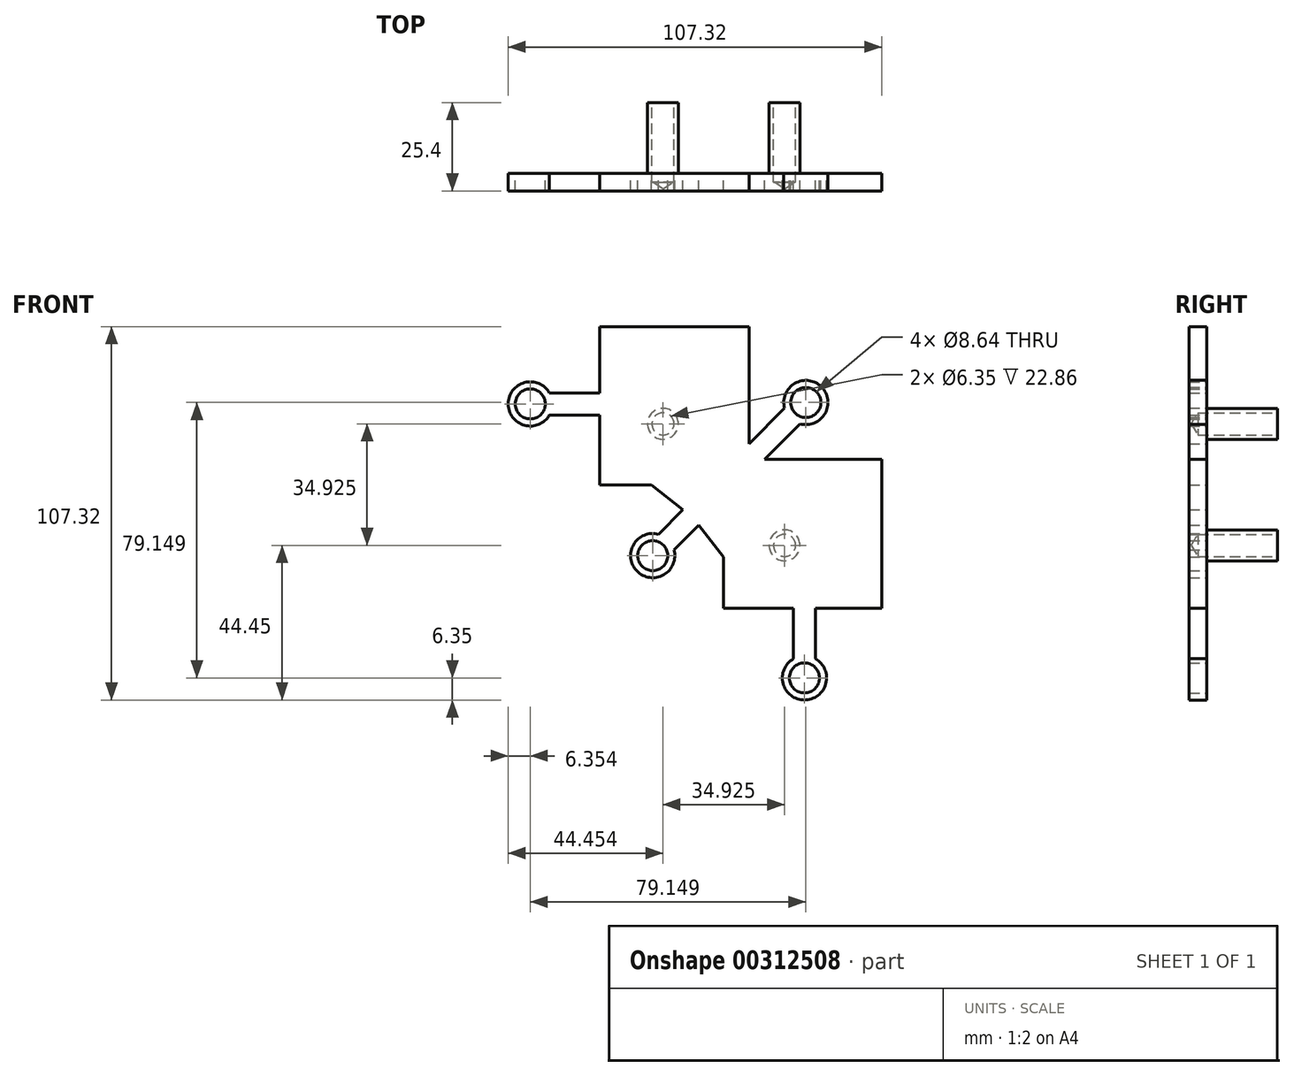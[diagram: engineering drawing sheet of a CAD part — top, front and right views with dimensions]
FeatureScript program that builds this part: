
annotation { "Feature Type Name" : "Feature", "Feature Type Description" : "" }
export const myFeature = defineFeature(function(context is Context, id is Id, definition is map)
    precondition{}
    {
        {
            var Q0;
            Q0=qCreatedBy(makeId("Front.planeOp"),FACE);
            var sketch = newSketch(context, id + "F0", { "sketchPlane" : qUnion([Q0])});
            skArc(sketch, "E0", {"start": v(27.13, 27.65) * mm, "mid": v(33.26, 38.27) * mm, "end": v(22.64, 32.14) * mm});
            skLineSegment(sketch, "E1.0", {"start": v(12.42, 21.92) * mm, "end": v(22.64, 32.14) * mm});
            skLineSegment(sketch, "E2.0", {"start": v(16.9, 17.43) * mm, "end": v(27.13, 27.65) * mm});
            skArc(sketch, "E3", {"start": v(-44.88, 36.55) * mm, "mid": v(-56.73, 33.37) * mm, "end": v(-44.88, 30.2) * mm});
            skArc(sketch, "E4", {"start": v(-13.58, -4.09) * mm, "mid": v(-19.71, -14.7) * mm, "end": v(-9.1, -8.58) * mm});
            skArc(sketch, "E5", {"start": v(25.19, -39.87) * mm, "mid": v(28.36, -51.72) * mm, "end": v(31.54, -39.87) * mm});
            skLineSegment(sketch, "E6.0", {"start": v(-44.88, 30.2) * mm, "end": v(-30.4, 30.2) * mm});
            skLineSegment(sketch, "E7.MirrorCS", {"start": v(25.19, -39.87) * mm, "end": v(25.19, -25.4) * mm});
            skArc(sketch, "E8.MirrorCS", {"start": v(31.54, -39.87) * mm, "mid": v(28.36, -51.72) * mm, "end": v(25.19, -39.87) * mm});
            skLineSegment(sketch, "E9", {"start": v(12.42, 36.55) * mm, "end": v(12.42, 21.92) * mm});
            skPoint(sketch, "E10.start.orphan", {"position": v(-7.83, 27.66) * mm});
            skLineSegment(sketch, "E11", {"start": v(31.54, 17.43) * mm, "end": v(16.9, 17.43) * mm});
            skPoint(sketch, "E12.start.orphan", {"position": v(22.65, -2.82) * mm});
            skLineSegment(sketch, "E13", {"start": v(31.54, -25.4) * mm, "end": v(31.54, -39.87) * mm});
            skLineSegment(sketch, "E14", {"start": v(-30.4, 36.55) * mm, "end": v(-44.88, 36.55) * mm});
            skLineSegment(sketch, "E15", {"start": v(-6.52, 2.97) * mm, "end": v(-15.61, 10.05) * mm});
            skPoint(sketch, "E15.endSnap0", {"position": v(-15.61, 24.72) * mm});
            skLineSegment(sketch, "E16", {"start": v(-15.61, 10.05) * mm, "end": v(-30.4, 10.05) * mm});
            skPoint(sketch, "E16.endSnap0", {"position": v(-30.4, 30.2) * mm});
            skLineSegment(sketch, "E17", {"start": v(-30.4, 16.4) * mm, "end": v(-30.4, 30.2) * mm});
            skCircle(sketch, "E18", {"center": v(-12.28, 27.66) * mm, "radius": 4.45 * mm});
            skLineSegment(sketch, "E19.MirrorCS", {"start": v(-2.03, -1.52) * mm, "end": v(5.05, -10.6) * mm});
            skLineSegment(sketch, "E20.MirrorCS", {"start": v(5.05, -10.6) * mm, "end": v(5.05, -25.4) * mm});
            skLineSegment(sketch, "E21.MirrorCS", {"start": v(11.4, -25.4) * mm, "end": v(25.19, -25.4) * mm});
            skCircle(sketch, "E22", {"center": v(22.65, -7.27) * mm, "radius": 4.45 * mm});
            skLineSegment(sketch, "E23.0", {"start": v(-9.1, -8.58) * mm, "end": v(-2.03, -1.52) * mm});
            skLineSegment(sketch, "E24.0", {"start": v(-13.58, -4.09) * mm, "end": v(-6.52, 2.97) * mm});
            skLineSegment(sketch, "E25", {"start": v(12.42, 36.55) * mm, "end": v(12.42, 55.6) * mm});
            skLineSegment(sketch, "E26", {"start": v(12.42, 55.6) * mm, "end": v(-30.4, 55.6) * mm});
            skLineSegment(sketch, "E27", {"start": v(-30.4, 55.6) * mm, "end": v(-30.4, 36.55) * mm});
            skLineSegment(sketch, "E28", {"start": v(-15.22, -10.22) * mm, "end": v(28.77, 33.78) * mm});
            skLineSegment(sketch, "E29.MirrorCS", {"start": v(50.59, 17.43) * mm, "end": v(50.59, -25.4) * mm});
            skLineSegment(sketch, "E30.MirrorCS", {"start": v(31.54, 17.43) * mm, "end": v(50.59, 17.43) * mm});
            skLineSegment(sketch, "E31.MirrorCS", {"start": v(50.59, -25.4) * mm, "end": v(31.54, -25.4) * mm});
            skLineSegment(sketch, "E32", {"start": v(-30.4, 16.4) * mm, "end": v(-30.4, 10.05) * mm});
            skLineSegment(sketch, "E33", {"start": v(5.05, -25.4) * mm, "end": v(11.4, -25.4) * mm});
            skPoint(sketch, "E34.end.orphan", {"position": v(-62.5, 16.4) * mm});
            skPoint(sketch, "E35.end.orphan", {"position": v(-62.5, -0.1) * mm});
            skPoint(sketch, "E36.end.orphan", {"position": v(-30.76, -0.1) * mm});
            skPoint(sketch, "E37.MirrorCS.end.orphan", {"position": v(-5.1, -25.75) * mm});
            skPoint(sketch, "E37.MirrorCS.start.orphan", {"position": v(5.05, -25.4) * mm});
            skPoint(sketch, "E38.MirrorCS.end.orphan", {"position": v(-5.1, -57.5) * mm});
            skPoint(sketch, "E39.MirrorCS.end.orphan", {"position": v(11.4, -57.5) * mm});
            skSolve(sketch);
        }
        {
            var Q0;
            Q0=makeQuery(id+"F0.imprint","IMPRINT",FACE,{"disambiguationData":[TD([[makeQuery(id+"F0.imprint","IMPRINT",EDGE,{"derivedFrom":sQuery(id+"F0.wireOp",EDGE,"E0")}),1.0]])]});
            extrude(context, id + "F1", {"entities" : qUnion([Q0]), "depth" : 5.08 * mm, "offsetDistance" : 25.4 * mm});
        }
        {
            var Q0;
            Q0=makeQuery(id+"F1.opExtrude","CAP_FACE",FACE,{"disambiguationData":[OSD([sQuery(id+"F0.wireOp",EDGE,"E0"),sQuery(id+"F0.wireOp",EDGE,"E1.0"),sQuery(id+"F0.wireOp",EDGE,"E2.0"),sQuery(id+"F0.wireOp",EDGE,"E3"),sQuery(id+"F0.wireOp",EDGE,"E4"),sQuery(id+"F0.wireOp",EDGE,"E6.0"),sQuery(id+"F0.wireOp",EDGE,"E7.MirrorCS"),sQuery(id+"F0.wireOp",EDGE,"E8.MirrorCS"),sQuery(id+"F0.wireOp",EDGE,"E9"),sQuery(id+"F0.wireOp",EDGE,"E11"),sQuery(id+"F0.wireOp",EDGE,"E13"),sQuery(id+"F0.wireOp",EDGE,"E14"),sQuery(id+"F0.wireOp",EDGE,"E15"),sQuery(id+"F0.wireOp",EDGE,"E16"),sQuery(id+"F0.wireOp",EDGE,"E17"),sQuery(id+"F0.wireOp",EDGE,"E18"),sQuery(id+"F0.wireOp",EDGE,"E19.MirrorCS"),sQuery(id+"F0.wireOp",EDGE,"E20.MirrorCS"),sQuery(id+"F0.wireOp",EDGE,"E21.MirrorCS"),sQuery(id+"F0.wireOp",EDGE,"E22"),sQuery(id+"F0.wireOp",EDGE,"E23.0"),sQuery(id+"F0.wireOp",EDGE,"E24.0"),sQuery(id+"F0.wireOp",EDGE,"E25"),sQuery(id+"F0.wireOp",EDGE,"E26"),sQuery(id+"F0.wireOp",EDGE,"E27"),sQuery(id+"F0.wireOp",EDGE,"E29.MirrorCS"),sQuery(id+"F0.wireOp",EDGE,"E30.MirrorCS"),sQuery(id+"F0.wireOp",EDGE,"E31.MirrorCS"),sQuery(id+"F0.wireOp",EDGE,"E32"),sQuery(id+"F0.wireOp",EDGE,"E33")])],"isStart":false});
            var sketch = newSketch(context, id + "F2", { "sketchPlane" : qUnion([Q0])});
            skCircle(sketch, "E40", {"center": v(-12.28, 27.66) * mm, "radius": 4.45 * mm});
            skCircle(sketch, "E41", {"center": v(22.65, -7.27) * mm, "radius": 4.45 * mm});
            skSolve(sketch);
        }
        {
            var Q0;
            Q0=makeQuery(id+"F2.imprint","IMPRINT",FACE,{"disambiguationData":[TD([[makeQuery(id+"F2.imprint","IMPRINT",EDGE,{"derivedFrom":sQuery(id+"F2.wireOp",EDGE,"E40")}),1.0]])]});
            var Q1;
            Q1=makeQuery(id+"F2.imprint","IMPRINT",FACE,{"disambiguationData":[TD([[makeQuery(id+"F2.imprint","IMPRINT",EDGE,{"derivedFrom":sQuery(id+"F2.wireOp",EDGE,"E41")}),1.0]])]});
            extrude(context, id + "F3", {"entities" : qUnion([Q0, Q1]), "operationType" : NewBodyOperationType.ADD, "oppositeDirection" : true, "depth" : 25.4 * mm, "offsetDistance" : 25.4 * mm});
        }
        {
            var Q0;
            Q0=makeQuery(id+"F1.opExtrude","CAP_FACE",FACE,{"disambiguationData":[OSD([sQuery(id+"F0.wireOp",EDGE,"E0"),sQuery(id+"F0.wireOp",EDGE,"E1.0"),sQuery(id+"F0.wireOp",EDGE,"E2.0"),sQuery(id+"F0.wireOp",EDGE,"E3"),sQuery(id+"F0.wireOp",EDGE,"E4"),sQuery(id+"F0.wireOp",EDGE,"E6.0"),sQuery(id+"F0.wireOp",EDGE,"E7.MirrorCS"),sQuery(id+"F0.wireOp",EDGE,"E8.MirrorCS"),sQuery(id+"F0.wireOp",EDGE,"E9"),sQuery(id+"F0.wireOp",EDGE,"E11"),sQuery(id+"F0.wireOp",EDGE,"E13"),sQuery(id+"F0.wireOp",EDGE,"E14"),sQuery(id+"F0.wireOp",EDGE,"E15"),sQuery(id+"F0.wireOp",EDGE,"E16"),sQuery(id+"F0.wireOp",EDGE,"E17"),sQuery(id+"F0.wireOp",EDGE,"E18"),sQuery(id+"F0.wireOp",EDGE,"E19.MirrorCS"),sQuery(id+"F0.wireOp",EDGE,"E20.MirrorCS"),sQuery(id+"F0.wireOp",EDGE,"E21.MirrorCS"),sQuery(id+"F0.wireOp",EDGE,"E22"),sQuery(id+"F0.wireOp",EDGE,"E23.0"),sQuery(id+"F0.wireOp",EDGE,"E24.0"),sQuery(id+"F0.wireOp",EDGE,"E25"),sQuery(id+"F0.wireOp",EDGE,"E26"),sQuery(id+"F0.wireOp",EDGE,"E27"),sQuery(id+"F0.wireOp",EDGE,"E29.MirrorCS"),sQuery(id+"F0.wireOp",EDGE,"E30.MirrorCS"),sQuery(id+"F0.wireOp",EDGE,"E31.MirrorCS"),sQuery(id+"F0.wireOp",EDGE,"E32"),sQuery(id+"F0.wireOp",EDGE,"E33")])],"isStart":true});
            var sketch = newSketch(context, id + "F4", { "sketchPlane" : qUnion([Q0])});
            skCircle(sketch, "E42", {"center": v(-28.36, -45.37) * mm, "radius": 4.32 * mm});
            skCircle(sketch, "E43", {"center": v(-28.77, 33.78) * mm, "radius": 4.32 * mm});
            skCircle(sketch, "E44", {"center": v(15.22, -10.22) * mm, "radius": 4.32 * mm});
            skCircle(sketch, "E45", {"center": v(50.38, 33.37) * mm, "radius": 4.32 * mm});
            skSolve(sketch);
        }
        {
            var Q0;
            Q0=makeQuery(id+"F4.imprint","IMPRINT",FACE,{"disambiguationData":[TD([[makeQuery(id+"F4.imprint","IMPRINT",EDGE,{"derivedFrom":sQuery(id+"F4.wireOp",EDGE,"E43")}),1.0]])]});
            var Q1;
            Q1=makeQuery(id+"F4.imprint","IMPRINT",FACE,{"disambiguationData":[TD([[makeQuery(id+"F4.imprint","IMPRINT",EDGE,{"derivedFrom":sQuery(id+"F4.wireOp",EDGE,"E44")}),1.0]])]});
            var Q2;
            Q2=makeQuery(id+"F4.imprint","IMPRINT",FACE,{"disambiguationData":[TD([[makeQuery(id+"F4.imprint","IMPRINT",EDGE,{"derivedFrom":sQuery(id+"F4.wireOp",EDGE,"E45")}),1.0]])]});
            var Q3;
            Q3=makeQuery(id+"F4.imprint","IMPRINT",FACE,{"disambiguationData":[TD([[makeQuery(id+"F4.imprint","IMPRINT",EDGE,{"derivedFrom":sQuery(id+"F4.wireOp",EDGE,"E42")}),1.0]])]});
            extrude(context, id + "F5", {"entities" : qUnion([Q0, Q1, Q2, Q3]), "operationType" : NewBodyOperationType.REMOVE, "oppositeDirection" : true, "depth" : 25.4 * mm, "offsetDistance" : 25.4 * mm});
        }
        {
            var Q0;
            Q0=makeQuery(id+"F3.opExtrude","CAP_FACE",FACE,{"disambiguationData":[OSD([sQuery(id+"F2.wireOp",EDGE,"E41")])],"isStart":false});
            var sketch = newSketch(context, id + "F6", { "sketchPlane" : qUnion([Q0])});
            skCircle(sketch, "E46", {"center": v(-22.65, -7.27) * mm, "radius": 3.18 * mm});
            skSolve(sketch);
        }
        {
            var Q0;
            Q0=makeQuery(id+"F3.opExtrude","CAP_FACE",FACE,{"disambiguationData":[OSD([sQuery(id+"F2.wireOp",EDGE,"E40")])],"isStart":false});
            var sketch = newSketch(context, id + "F7", { "sketchPlane" : qUnion([Q0])});
            skCircle(sketch, "E47", {"center": v(12.28, 27.66) * mm, "radius": 3.18 * mm});
            skSolve(sketch);
        }
        {
            var Q0;
            Q0=sQuery(id+"F6.wireOp",VERTEX,"E46.center");
            var Q1;
            Q1=sQuery(id+"F7.wireOp",VERTEX,"E47.center");
            var Q2;
            Q2=makeQuery(id+"F1.opExtrude","SWEPT_BODY",BODY,{"disambiguationData":[OSD([sQuery(id+"F0.wireOp",EDGE,"E0"),sQuery(id+"F0.wireOp",EDGE,"E1.0"),sQuery(id+"F0.wireOp",EDGE,"E2.0"),sQuery(id+"F0.wireOp",EDGE,"E3"),sQuery(id+"F0.wireOp",EDGE,"E4"),sQuery(id+"F0.wireOp",EDGE,"E6.0"),sQuery(id+"F0.wireOp",EDGE,"E7.MirrorCS"),sQuery(id+"F0.wireOp",EDGE,"E8.MirrorCS"),sQuery(id+"F0.wireOp",EDGE,"E9"),sQuery(id+"F0.wireOp",EDGE,"E11"),sQuery(id+"F0.wireOp",EDGE,"E13"),sQuery(id+"F0.wireOp",EDGE,"E14"),sQuery(id+"F0.wireOp",EDGE,"E15"),sQuery(id+"F0.wireOp",EDGE,"E16"),sQuery(id+"F0.wireOp",EDGE,"E17"),sQuery(id+"F0.wireOp",EDGE,"E18"),sQuery(id+"F0.wireOp",EDGE,"E19.MirrorCS"),sQuery(id+"F0.wireOp",EDGE,"E20.MirrorCS"),sQuery(id+"F0.wireOp",EDGE,"E21.MirrorCS"),sQuery(id+"F0.wireOp",EDGE,"E22"),sQuery(id+"F0.wireOp",EDGE,"E23.0"),sQuery(id+"F0.wireOp",EDGE,"E24.0"),sQuery(id+"F0.wireOp",EDGE,"E25"),sQuery(id+"F0.wireOp",EDGE,"E26"),sQuery(id+"F0.wireOp",EDGE,"E27"),sQuery(id+"F0.wireOp",EDGE,"E29.MirrorCS"),sQuery(id+"F0.wireOp",EDGE,"E30.MirrorCS"),sQuery(id+"F0.wireOp",EDGE,"E31.MirrorCS"),sQuery(id+"F0.wireOp",EDGE,"E32"),sQuery(id+"F0.wireOp",EDGE,"E33")])]});
            hole(context, id + "F8", {"style" : HoleStyle.C_BORE, "endStyle" : HoleEndStyle.BLIND, "holeDiameter" : 6.35 * mm, "cBoreDiameter" : 6.35 * mm, "cBoreDepth" : 12.7 * mm, "majorDiameter" : 6.35 * mm, "holeDepth" : 22.86 * mm, "isTappedThrough" : true, "tappedDepth" : 12.7 * mm, "tapClearance" : 3, "locations" : qUnion([Q0, Q1]), "scope" : qUnion([Q2])});
        }
    });
